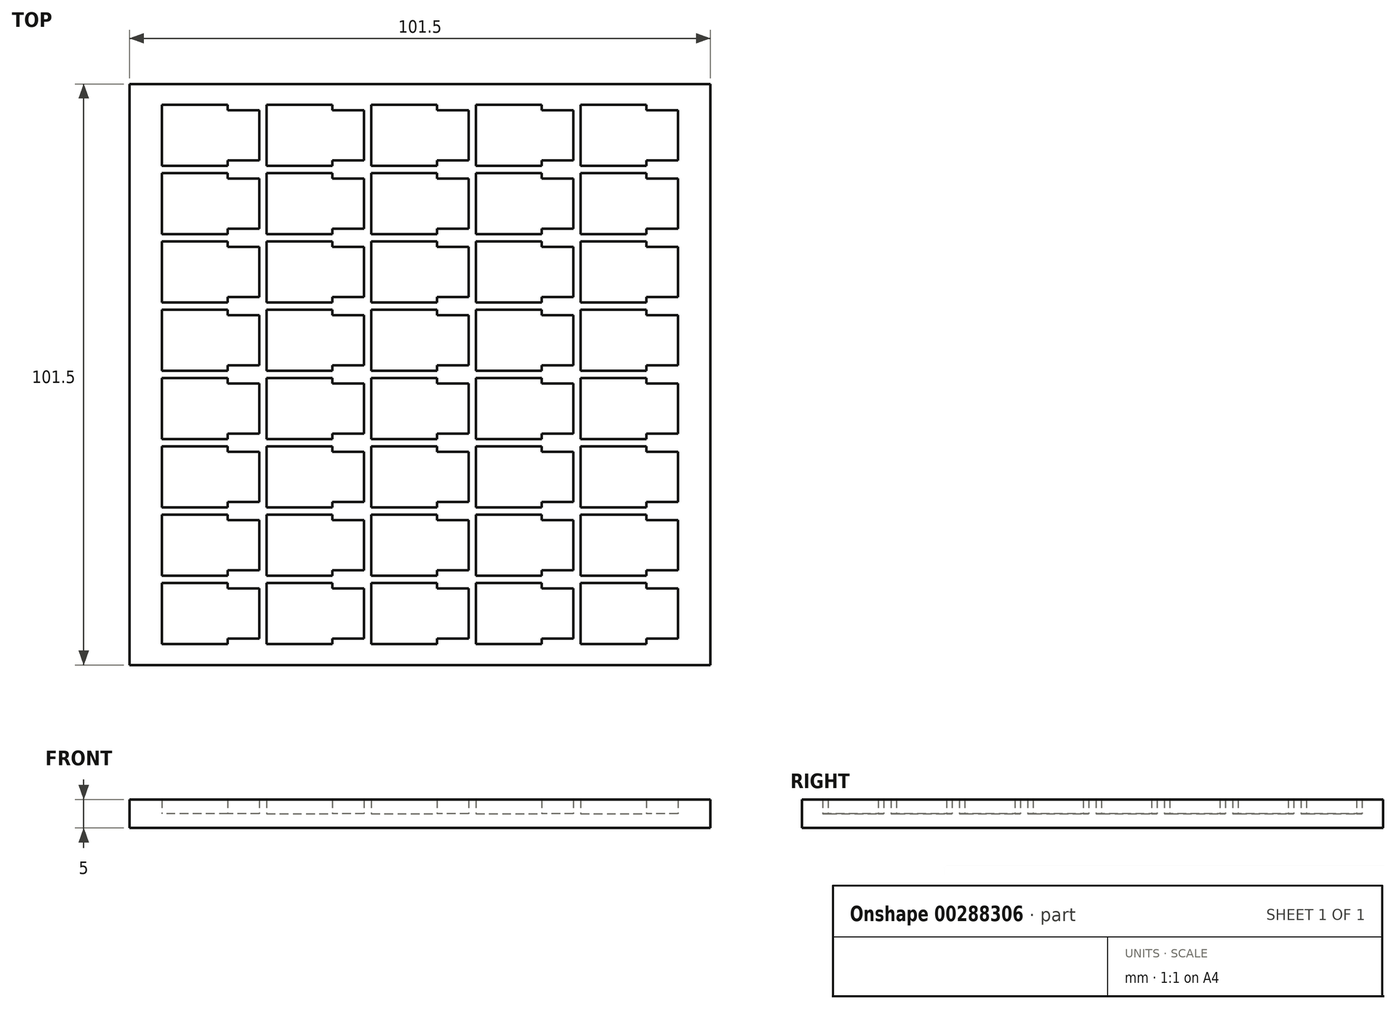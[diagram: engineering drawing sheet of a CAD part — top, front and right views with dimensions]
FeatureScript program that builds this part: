
annotation { "Feature Type Name" : "Feature", "Feature Type Description" : "" }
export const myFeature = defineFeature(function(context is Context, id is Id, definition is map)
    precondition{}
    {
        {
            var Q0;
            Q0=qCreatedBy(makeId("Top.planeOp"),FACE);
            var sketch = newSketch(context, id + "F0", { "sketchPlane" : qUnion([Q0])});
            skLineSegment(sketch, "E0.bottom", {"start": v(50.75, -50.75) * mm, "end": v(-50.75, -50.75) * mm});
            skLineSegment(sketch, "E0.top", {"start": v(50.75, 50.75) * mm, "end": v(-50.75, 50.75) * mm});
            skLineSegment(sketch, "E0.left", {"start": v(50.75, -50.75) * mm, "end": v(50.75, 50.75) * mm});
            skLineSegment(sketch, "E0.right", {"start": v(-50.75, -50.75) * mm, "end": v(-50.75, 50.75) * mm});
            skPoint(sketch, "E0.middle", {"position": v(0, 0) * mm});
            skLineSegment(sketch, "E1", {"start": v(-45.07, 47.12) * mm, "end": v(-45.07, 36.45) * mm});
            skLineSegment(sketch, "E2", {"start": v(-45.07, 36.45) * mm, "end": v(-33.57, 36.45) * mm});
            skLineSegment(sketch, "E3", {"start": v(-33.57, 36.45) * mm, "end": v(-33.57, 37.4) * mm});
            skLineSegment(sketch, "E4", {"start": v(-33.57, 37.4) * mm, "end": v(-28.07, 37.4) * mm});
            skLineSegment(sketch, "E5", {"start": v(-28.07, 37.4) * mm, "end": v(-28.07, 46.16) * mm});
            skLineSegment(sketch, "E6", {"start": v(-28.07, 46.16) * mm, "end": v(-33.57, 46.16) * mm});
            skLineSegment(sketch, "E7", {"start": v(-33.57, 46.16) * mm, "end": v(-33.57, 47.12) * mm});
            skLineSegment(sketch, "E8", {"start": v(-33.57, 47.12) * mm, "end": v(-45.07, 47.12) * mm});
            skLineSegment(sketch, "E9.0.1.0", {"start": v(-33.57, 24.5) * mm, "end": v(-33.57, 25.46) * mm});
            skLineSegment(sketch, "E9.0.1.1", {"start": v(-45.07, 24.5) * mm, "end": v(-33.57, 24.5) * mm});
            skLineSegment(sketch, "E9.0.1.2", {"start": v(-28.07, 25.46) * mm, "end": v(-28.07, 34.23) * mm});
            skLineSegment(sketch, "E9.0.1.3", {"start": v(-33.57, 34.23) * mm, "end": v(-33.57, 35.18) * mm});
            skLineSegment(sketch, "E9.0.1.4", {"start": v(-33.57, 25.46) * mm, "end": v(-28.07, 25.46) * mm});
            skLineSegment(sketch, "E9.0.1.5", {"start": v(-45.07, 35.18) * mm, "end": v(-45.07, 24.5) * mm});
            skLineSegment(sketch, "E9.0.1.6", {"start": v(-33.57, 35.18) * mm, "end": v(-45.07, 35.18) * mm});
            skLineSegment(sketch, "E9.0.1.7", {"start": v(-28.07, 34.23) * mm, "end": v(-33.57, 34.23) * mm});
            skLineSegment(sketch, "E9.0.2.0", {"start": v(-33.57, 12.57) * mm, "end": v(-33.57, 13.53) * mm});
            skLineSegment(sketch, "E9.0.2.1", {"start": v(-45.07, 12.57) * mm, "end": v(-33.57, 12.57) * mm});
            skLineSegment(sketch, "E9.0.2.2", {"start": v(-28.07, 13.53) * mm, "end": v(-28.07, 22.29) * mm});
            skLineSegment(sketch, "E9.0.2.3", {"start": v(-33.57, 22.29) * mm, "end": v(-33.57, 23.24) * mm});
            skLineSegment(sketch, "E9.0.2.4", {"start": v(-33.57, 13.53) * mm, "end": v(-28.07, 13.53) * mm});
            skLineSegment(sketch, "E9.0.2.5", {"start": v(-45.07, 23.24) * mm, "end": v(-45.07, 12.57) * mm});
            skLineSegment(sketch, "E9.0.2.6", {"start": v(-33.57, 23.24) * mm, "end": v(-45.07, 23.24) * mm});
            skLineSegment(sketch, "E9.0.2.7", {"start": v(-28.07, 22.29) * mm, "end": v(-33.57, 22.29) * mm});
            skLineSegment(sketch, "E9.0.3.0", {"start": v(-33.57, 0.63) * mm, "end": v(-33.57, 1.59) * mm});
            skLineSegment(sketch, "E9.0.3.1", {"start": v(-45.07, 0.63) * mm, "end": v(-33.57, 0.63) * mm});
            skLineSegment(sketch, "E9.0.3.2", {"start": v(-28.07, 1.59) * mm, "end": v(-28.07, 10.35) * mm});
            skLineSegment(sketch, "E9.0.3.3", {"start": v(-33.57, 10.35) * mm, "end": v(-33.57, 11.3) * mm});
            skLineSegment(sketch, "E9.0.3.4", {"start": v(-33.57, 1.59) * mm, "end": v(-28.07, 1.59) * mm});
            skLineSegment(sketch, "E9.0.3.5", {"start": v(-45.07, 11.3) * mm, "end": v(-45.07, 0.63) * mm});
            skLineSegment(sketch, "E9.0.3.6", {"start": v(-33.57, 11.3) * mm, "end": v(-45.07, 11.3) * mm});
            skLineSegment(sketch, "E9.0.3.7", {"start": v(-28.07, 10.35) * mm, "end": v(-33.57, 10.35) * mm});
            skLineSegment(sketch, "E9.0.4.0", {"start": v(-33.57, -11.3) * mm, "end": v(-33.57, -10.35) * mm});
            skLineSegment(sketch, "E9.0.4.1", {"start": v(-45.07, -11.3) * mm, "end": v(-33.57, -11.3) * mm});
            skLineSegment(sketch, "E9.0.4.2", {"start": v(-28.07, -10.35) * mm, "end": v(-28.07, -1.59) * mm});
            skLineSegment(sketch, "E9.0.4.3", {"start": v(-33.57, -1.59) * mm, "end": v(-33.57, -0.63) * mm});
            skLineSegment(sketch, "E9.0.4.4", {"start": v(-33.57, -10.35) * mm, "end": v(-28.07, -10.35) * mm});
            skLineSegment(sketch, "E9.0.4.5", {"start": v(-45.07, -0.63) * mm, "end": v(-45.07, -11.3) * mm});
            skLineSegment(sketch, "E9.0.4.6", {"start": v(-33.57, -0.63) * mm, "end": v(-45.07, -0.63) * mm});
            skLineSegment(sketch, "E9.0.4.7", {"start": v(-28.07, -1.59) * mm, "end": v(-33.57, -1.59) * mm});
            skLineSegment(sketch, "E9.0.5.0", {"start": v(-33.57, -23.24) * mm, "end": v(-33.57, -22.29) * mm});
            skLineSegment(sketch, "E9.0.5.1", {"start": v(-45.07, -23.24) * mm, "end": v(-33.57, -23.24) * mm});
            skLineSegment(sketch, "E9.0.5.2", {"start": v(-28.07, -22.29) * mm, "end": v(-28.07, -13.53) * mm});
            skLineSegment(sketch, "E9.0.5.3", {"start": v(-33.57, -13.53) * mm, "end": v(-33.57, -12.57) * mm});
            skLineSegment(sketch, "E9.0.5.4", {"start": v(-33.57, -22.29) * mm, "end": v(-28.07, -22.29) * mm});
            skLineSegment(sketch, "E9.0.5.5", {"start": v(-45.07, -12.57) * mm, "end": v(-45.07, -23.24) * mm});
            skLineSegment(sketch, "E9.0.5.6", {"start": v(-33.57, -12.57) * mm, "end": v(-45.07, -12.57) * mm});
            skLineSegment(sketch, "E9.0.5.7", {"start": v(-28.07, -13.53) * mm, "end": v(-33.57, -13.53) * mm});
            skLineSegment(sketch, "E9.0.6.0", {"start": v(-33.57, -35.18) * mm, "end": v(-33.57, -34.23) * mm});
            skLineSegment(sketch, "E9.0.6.1", {"start": v(-45.07, -35.18) * mm, "end": v(-33.57, -35.18) * mm});
            skLineSegment(sketch, "E9.0.6.2", {"start": v(-28.07, -34.23) * mm, "end": v(-28.07, -25.46) * mm});
            skLineSegment(sketch, "E9.0.6.3", {"start": v(-33.57, -25.46) * mm, "end": v(-33.57, -24.51) * mm});
            skLineSegment(sketch, "E9.0.6.4", {"start": v(-33.57, -34.23) * mm, "end": v(-28.07, -34.23) * mm});
            skLineSegment(sketch, "E9.0.6.5", {"start": v(-45.07, -24.51) * mm, "end": v(-45.07, -35.18) * mm});
            skLineSegment(sketch, "E9.0.6.6", {"start": v(-33.57, -24.51) * mm, "end": v(-45.07, -24.51) * mm});
            skLineSegment(sketch, "E9.0.6.7", {"start": v(-28.07, -25.46) * mm, "end": v(-33.57, -25.46) * mm});
            skLineSegment(sketch, "E9.0.7.0", {"start": v(-33.57, -47.12) * mm, "end": v(-33.57, -46.16) * mm});
            skLineSegment(sketch, "E9.0.7.1", {"start": v(-45.07, -47.12) * mm, "end": v(-33.57, -47.12) * mm});
            skLineSegment(sketch, "E9.0.7.2", {"start": v(-28.07, -46.16) * mm, "end": v(-28.07, -37.4) * mm});
            skLineSegment(sketch, "E9.0.7.3", {"start": v(-33.57, -37.4) * mm, "end": v(-33.57, -36.45) * mm});
            skLineSegment(sketch, "E9.0.7.4", {"start": v(-33.57, -46.16) * mm, "end": v(-28.07, -46.16) * mm});
            skLineSegment(sketch, "E9.0.7.5", {"start": v(-45.07, -36.45) * mm, "end": v(-45.07, -47.12) * mm});
            skLineSegment(sketch, "E9.0.7.6", {"start": v(-33.57, -36.45) * mm, "end": v(-45.07, -36.45) * mm});
            skLineSegment(sketch, "E9.0.7.7", {"start": v(-28.07, -37.4) * mm, "end": v(-33.57, -37.4) * mm});
            skLineSegment(sketch, "E9.1.0.0", {"start": v(-15.29, 36.45) * mm, "end": v(-15.29, 37.4) * mm});
            skLineSegment(sketch, "E9.1.0.1", {"start": v(-26.79, 36.45) * mm, "end": v(-15.29, 36.45) * mm});
            skLineSegment(sketch, "E9.1.0.2", {"start": v(-9.79, 37.4) * mm, "end": v(-9.79, 46.16) * mm});
            skLineSegment(sketch, "E9.1.0.3", {"start": v(-15.29, 46.16) * mm, "end": v(-15.29, 47.12) * mm});
            skLineSegment(sketch, "E9.1.0.4", {"start": v(-15.29, 37.4) * mm, "end": v(-9.79, 37.4) * mm});
            skLineSegment(sketch, "E9.1.0.5", {"start": v(-26.79, 47.12) * mm, "end": v(-26.79, 36.45) * mm});
            skLineSegment(sketch, "E9.1.0.6", {"start": v(-15.29, 47.12) * mm, "end": v(-26.79, 47.12) * mm});
            skLineSegment(sketch, "E9.1.0.7", {"start": v(-9.79, 46.16) * mm, "end": v(-15.29, 46.16) * mm});
            skLineSegment(sketch, "E9.1.1.0", {"start": v(-15.29, 24.5) * mm, "end": v(-15.29, 25.46) * mm});
            skLineSegment(sketch, "E9.1.1.1", {"start": v(-26.79, 24.5) * mm, "end": v(-15.29, 24.5) * mm});
            skLineSegment(sketch, "E9.1.1.2", {"start": v(-9.79, 25.46) * mm, "end": v(-9.79, 34.23) * mm});
            skLineSegment(sketch, "E9.1.1.3", {"start": v(-15.29, 34.23) * mm, "end": v(-15.29, 35.18) * mm});
            skLineSegment(sketch, "E9.1.1.4", {"start": v(-15.29, 25.46) * mm, "end": v(-9.79, 25.46) * mm});
            skLineSegment(sketch, "E9.1.1.5", {"start": v(-26.79, 35.18) * mm, "end": v(-26.79, 24.5) * mm});
            skLineSegment(sketch, "E9.1.1.6", {"start": v(-15.29, 35.18) * mm, "end": v(-26.79, 35.18) * mm});
            skLineSegment(sketch, "E9.1.1.7", {"start": v(-9.79, 34.23) * mm, "end": v(-15.29, 34.23) * mm});
            skLineSegment(sketch, "E9.1.2.0", {"start": v(-15.29, 12.57) * mm, "end": v(-15.29, 13.53) * mm});
            skLineSegment(sketch, "E9.1.2.1", {"start": v(-26.79, 12.57) * mm, "end": v(-15.29, 12.57) * mm});
            skLineSegment(sketch, "E9.1.2.2", {"start": v(-9.79, 13.53) * mm, "end": v(-9.79, 22.29) * mm});
            skLineSegment(sketch, "E9.1.2.3", {"start": v(-15.29, 22.29) * mm, "end": v(-15.29, 23.24) * mm});
            skLineSegment(sketch, "E9.1.2.4", {"start": v(-15.29, 13.53) * mm, "end": v(-9.79, 13.53) * mm});
            skLineSegment(sketch, "E9.1.2.5", {"start": v(-26.79, 23.24) * mm, "end": v(-26.79, 12.57) * mm});
            skLineSegment(sketch, "E9.1.2.6", {"start": v(-15.29, 23.24) * mm, "end": v(-26.79, 23.24) * mm});
            skLineSegment(sketch, "E9.1.2.7", {"start": v(-9.79, 22.29) * mm, "end": v(-15.29, 22.29) * mm});
            skLineSegment(sketch, "E9.1.3.0", {"start": v(-15.29, 0.63) * mm, "end": v(-15.29, 1.59) * mm});
            skLineSegment(sketch, "E9.1.3.1", {"start": v(-26.79, 0.63) * mm, "end": v(-15.29, 0.63) * mm});
            skLineSegment(sketch, "E9.1.3.2", {"start": v(-9.79, 1.59) * mm, "end": v(-9.79, 10.35) * mm});
            skLineSegment(sketch, "E9.1.3.3", {"start": v(-15.29, 10.35) * mm, "end": v(-15.29, 11.3) * mm});
            skLineSegment(sketch, "E9.1.3.4", {"start": v(-15.29, 1.59) * mm, "end": v(-9.79, 1.59) * mm});
            skLineSegment(sketch, "E9.1.3.5", {"start": v(-26.79, 11.3) * mm, "end": v(-26.79, 0.63) * mm});
            skLineSegment(sketch, "E9.1.3.6", {"start": v(-15.29, 11.3) * mm, "end": v(-26.79, 11.3) * mm});
            skLineSegment(sketch, "E9.1.3.7", {"start": v(-9.79, 10.35) * mm, "end": v(-15.29, 10.35) * mm});
            skLineSegment(sketch, "E9.1.4.0", {"start": v(-15.29, -11.3) * mm, "end": v(-15.29, -10.35) * mm});
            skLineSegment(sketch, "E9.1.4.1", {"start": v(-26.79, -11.3) * mm, "end": v(-15.29, -11.3) * mm});
            skLineSegment(sketch, "E9.1.4.2", {"start": v(-9.79, -10.35) * mm, "end": v(-9.79, -1.59) * mm});
            skLineSegment(sketch, "E9.1.4.3", {"start": v(-15.29, -1.59) * mm, "end": v(-15.29, -0.63) * mm});
            skLineSegment(sketch, "E9.1.4.4", {"start": v(-15.29, -10.35) * mm, "end": v(-9.79, -10.35) * mm});
            skLineSegment(sketch, "E9.1.4.5", {"start": v(-26.79, -0.63) * mm, "end": v(-26.79, -11.3) * mm});
            skLineSegment(sketch, "E9.1.4.6", {"start": v(-15.29, -0.63) * mm, "end": v(-26.79, -0.63) * mm});
            skLineSegment(sketch, "E9.1.4.7", {"start": v(-9.79, -1.59) * mm, "end": v(-15.29, -1.59) * mm});
            skLineSegment(sketch, "E9.1.5.0", {"start": v(-15.29, -23.24) * mm, "end": v(-15.29, -22.29) * mm});
            skLineSegment(sketch, "E9.1.5.1", {"start": v(-26.79, -23.24) * mm, "end": v(-15.29, -23.24) * mm});
            skLineSegment(sketch, "E9.1.5.2", {"start": v(-9.79, -22.29) * mm, "end": v(-9.79, -13.53) * mm});
            skLineSegment(sketch, "E9.1.5.3", {"start": v(-15.29, -13.53) * mm, "end": v(-15.29, -12.57) * mm});
            skLineSegment(sketch, "E9.1.5.4", {"start": v(-15.29, -22.29) * mm, "end": v(-9.79, -22.29) * mm});
            skLineSegment(sketch, "E9.1.5.5", {"start": v(-26.79, -12.57) * mm, "end": v(-26.79, -23.24) * mm});
            skLineSegment(sketch, "E9.1.5.6", {"start": v(-15.29, -12.57) * mm, "end": v(-26.79, -12.57) * mm});
            skLineSegment(sketch, "E9.1.5.7", {"start": v(-9.79, -13.53) * mm, "end": v(-15.29, -13.53) * mm});
            skLineSegment(sketch, "E9.1.6.0", {"start": v(-15.29, -35.18) * mm, "end": v(-15.29, -34.23) * mm});
            skLineSegment(sketch, "E9.1.6.1", {"start": v(-26.79, -35.18) * mm, "end": v(-15.29, -35.18) * mm});
            skLineSegment(sketch, "E9.1.6.2", {"start": v(-9.79, -34.23) * mm, "end": v(-9.79, -25.46) * mm});
            skLineSegment(sketch, "E9.1.6.3", {"start": v(-15.29, -25.46) * mm, "end": v(-15.29, -24.51) * mm});
            skLineSegment(sketch, "E9.1.6.4", {"start": v(-15.29, -34.23) * mm, "end": v(-9.79, -34.23) * mm});
            skLineSegment(sketch, "E9.1.6.5", {"start": v(-26.79, -24.51) * mm, "end": v(-26.79, -35.18) * mm});
            skLineSegment(sketch, "E9.1.6.6", {"start": v(-15.29, -24.51) * mm, "end": v(-26.79, -24.51) * mm});
            skLineSegment(sketch, "E9.1.6.7", {"start": v(-9.79, -25.46) * mm, "end": v(-15.29, -25.46) * mm});
            skLineSegment(sketch, "E9.1.7.0", {"start": v(-15.29, -47.12) * mm, "end": v(-15.29, -46.16) * mm});
            skLineSegment(sketch, "E9.1.7.1", {"start": v(-26.79, -47.12) * mm, "end": v(-15.29, -47.12) * mm});
            skLineSegment(sketch, "E9.1.7.2", {"start": v(-9.79, -46.16) * mm, "end": v(-9.79, -37.4) * mm});
            skLineSegment(sketch, "E9.1.7.3", {"start": v(-15.29, -37.4) * mm, "end": v(-15.29, -36.45) * mm});
            skLineSegment(sketch, "E9.1.7.4", {"start": v(-15.29, -46.16) * mm, "end": v(-9.79, -46.16) * mm});
            skLineSegment(sketch, "E9.1.7.5", {"start": v(-26.79, -36.45) * mm, "end": v(-26.79, -47.12) * mm});
            skLineSegment(sketch, "E9.1.7.6", {"start": v(-15.29, -36.45) * mm, "end": v(-26.79, -36.45) * mm});
            skLineSegment(sketch, "E9.1.7.7", {"start": v(-9.79, -37.4) * mm, "end": v(-15.29, -37.4) * mm});
            skLineSegment(sketch, "E9.2.0.0", {"start": v(3, 36.45) * mm, "end": v(3, 37.4) * mm});
            skLineSegment(sketch, "E9.2.0.1", {"start": v(-8.5, 36.45) * mm, "end": v(3, 36.45) * mm});
            skLineSegment(sketch, "E9.2.0.2", {"start": v(8.5, 37.4) * mm, "end": v(8.5, 46.16) * mm});
            skLineSegment(sketch, "E9.2.0.3", {"start": v(3, 46.16) * mm, "end": v(3, 47.12) * mm});
            skLineSegment(sketch, "E9.2.0.4", {"start": v(3, 37.4) * mm, "end": v(8.5, 37.4) * mm});
            skLineSegment(sketch, "E9.2.0.5", {"start": v(-8.5, 47.12) * mm, "end": v(-8.5, 36.45) * mm});
            skLineSegment(sketch, "E9.2.0.6", {"start": v(3, 47.12) * mm, "end": v(-8.5, 47.12) * mm});
            skLineSegment(sketch, "E9.2.0.7", {"start": v(8.5, 46.16) * mm, "end": v(3, 46.16) * mm});
            skLineSegment(sketch, "E9.2.1.0", {"start": v(3, 24.5) * mm, "end": v(3, 25.46) * mm});
            skLineSegment(sketch, "E9.2.1.1", {"start": v(-8.5, 24.5) * mm, "end": v(3, 24.5) * mm});
            skLineSegment(sketch, "E9.2.1.2", {"start": v(8.5, 25.46) * mm, "end": v(8.5, 34.23) * mm});
            skLineSegment(sketch, "E9.2.1.3", {"start": v(3, 34.23) * mm, "end": v(3, 35.18) * mm});
            skLineSegment(sketch, "E9.2.1.4", {"start": v(3, 25.46) * mm, "end": v(8.5, 25.46) * mm});
            skLineSegment(sketch, "E9.2.1.5", {"start": v(-8.5, 35.18) * mm, "end": v(-8.5, 24.5) * mm});
            skLineSegment(sketch, "E9.2.1.6", {"start": v(3, 35.18) * mm, "end": v(-8.5, 35.18) * mm});
            skLineSegment(sketch, "E9.2.1.7", {"start": v(8.5, 34.23) * mm, "end": v(3, 34.23) * mm});
            skLineSegment(sketch, "E9.2.2.0", {"start": v(3, 12.57) * mm, "end": v(3, 13.53) * mm});
            skLineSegment(sketch, "E9.2.2.1", {"start": v(-8.5, 12.57) * mm, "end": v(3, 12.57) * mm});
            skLineSegment(sketch, "E9.2.2.2", {"start": v(8.5, 13.53) * mm, "end": v(8.5, 22.29) * mm});
            skLineSegment(sketch, "E9.2.2.3", {"start": v(3, 22.29) * mm, "end": v(3, 23.24) * mm});
            skLineSegment(sketch, "E9.2.2.4", {"start": v(3, 13.53) * mm, "end": v(8.5, 13.53) * mm});
            skLineSegment(sketch, "E9.2.2.5", {"start": v(-8.5, 23.24) * mm, "end": v(-8.5, 12.57) * mm});
            skLineSegment(sketch, "E9.2.2.6", {"start": v(3, 23.24) * mm, "end": v(-8.5, 23.24) * mm});
            skLineSegment(sketch, "E9.2.2.7", {"start": v(8.5, 22.29) * mm, "end": v(3, 22.29) * mm});
            skLineSegment(sketch, "E9.2.3.0", {"start": v(3, 0.63) * mm, "end": v(3, 1.59) * mm});
            skLineSegment(sketch, "E9.2.3.1", {"start": v(-8.5, 0.63) * mm, "end": v(3, 0.63) * mm});
            skLineSegment(sketch, "E9.2.3.2", {"start": v(8.5, 1.59) * mm, "end": v(8.5, 10.35) * mm});
            skLineSegment(sketch, "E9.2.3.3", {"start": v(3, 10.35) * mm, "end": v(3, 11.3) * mm});
            skLineSegment(sketch, "E9.2.3.4", {"start": v(3, 1.59) * mm, "end": v(8.5, 1.59) * mm});
            skLineSegment(sketch, "E9.2.3.5", {"start": v(-8.5, 11.3) * mm, "end": v(-8.5, 0.63) * mm});
            skLineSegment(sketch, "E9.2.3.6", {"start": v(3, 11.3) * mm, "end": v(-8.5, 11.3) * mm});
            skLineSegment(sketch, "E9.2.3.7", {"start": v(8.5, 10.35) * mm, "end": v(3, 10.35) * mm});
            skLineSegment(sketch, "E9.2.4.0", {"start": v(3, -11.3) * mm, "end": v(3, -10.35) * mm});
            skLineSegment(sketch, "E9.2.4.1", {"start": v(-8.5, -11.3) * mm, "end": v(3, -11.3) * mm});
            skLineSegment(sketch, "E9.2.4.2", {"start": v(8.5, -10.35) * mm, "end": v(8.5, -1.59) * mm});
            skLineSegment(sketch, "E9.2.4.3", {"start": v(3, -1.59) * mm, "end": v(3, -0.63) * mm});
            skLineSegment(sketch, "E9.2.4.4", {"start": v(3, -10.35) * mm, "end": v(8.5, -10.35) * mm});
            skLineSegment(sketch, "E9.2.4.5", {"start": v(-8.5, -0.63) * mm, "end": v(-8.5, -11.3) * mm});
            skLineSegment(sketch, "E9.2.4.6", {"start": v(3, -0.63) * mm, "end": v(-8.5, -0.63) * mm});
            skLineSegment(sketch, "E9.2.4.7", {"start": v(8.5, -1.59) * mm, "end": v(3, -1.59) * mm});
            skLineSegment(sketch, "E9.2.5.0", {"start": v(3, -23.24) * mm, "end": v(3, -22.29) * mm});
            skLineSegment(sketch, "E9.2.5.1", {"start": v(-8.5, -23.24) * mm, "end": v(3, -23.24) * mm});
            skLineSegment(sketch, "E9.2.5.2", {"start": v(8.5, -22.29) * mm, "end": v(8.5, -13.53) * mm});
            skLineSegment(sketch, "E9.2.5.3", {"start": v(3, -13.53) * mm, "end": v(3, -12.57) * mm});
            skLineSegment(sketch, "E9.2.5.4", {"start": v(3, -22.29) * mm, "end": v(8.5, -22.29) * mm});
            skLineSegment(sketch, "E9.2.5.5", {"start": v(-8.5, -12.57) * mm, "end": v(-8.5, -23.24) * mm});
            skLineSegment(sketch, "E9.2.5.6", {"start": v(3, -12.57) * mm, "end": v(-8.5, -12.57) * mm});
            skLineSegment(sketch, "E9.2.5.7", {"start": v(8.5, -13.53) * mm, "end": v(3, -13.53) * mm});
            skLineSegment(sketch, "E9.2.6.0", {"start": v(3, -35.18) * mm, "end": v(3, -34.23) * mm});
            skLineSegment(sketch, "E9.2.6.1", {"start": v(-8.5, -35.18) * mm, "end": v(3, -35.18) * mm});
            skLineSegment(sketch, "E9.2.6.2", {"start": v(8.5, -34.23) * mm, "end": v(8.5, -25.46) * mm});
            skLineSegment(sketch, "E9.2.6.3", {"start": v(3, -25.46) * mm, "end": v(3, -24.51) * mm});
            skLineSegment(sketch, "E9.2.6.4", {"start": v(3, -34.23) * mm, "end": v(8.5, -34.23) * mm});
            skLineSegment(sketch, "E9.2.6.5", {"start": v(-8.5, -24.51) * mm, "end": v(-8.5, -35.18) * mm});
            skLineSegment(sketch, "E9.2.6.6", {"start": v(3, -24.51) * mm, "end": v(-8.5, -24.51) * mm});
            skLineSegment(sketch, "E9.2.6.7", {"start": v(8.5, -25.46) * mm, "end": v(3, -25.46) * mm});
            skLineSegment(sketch, "E9.2.7.0", {"start": v(3, -47.12) * mm, "end": v(3, -46.16) * mm});
            skLineSegment(sketch, "E9.2.7.1", {"start": v(-8.5, -47.12) * mm, "end": v(3, -47.12) * mm});
            skLineSegment(sketch, "E9.2.7.2", {"start": v(8.5, -46.16) * mm, "end": v(8.5, -37.4) * mm});
            skLineSegment(sketch, "E9.2.7.3", {"start": v(3, -37.4) * mm, "end": v(3, -36.45) * mm});
            skLineSegment(sketch, "E9.2.7.4", {"start": v(3, -46.16) * mm, "end": v(8.5, -46.16) * mm});
            skLineSegment(sketch, "E9.2.7.5", {"start": v(-8.5, -36.45) * mm, "end": v(-8.5, -47.12) * mm});
            skLineSegment(sketch, "E9.2.7.6", {"start": v(3, -36.45) * mm, "end": v(-8.5, -36.45) * mm});
            skLineSegment(sketch, "E9.2.7.7", {"start": v(8.5, -37.4) * mm, "end": v(3, -37.4) * mm});
            skLineSegment(sketch, "E9.3.0.0", {"start": v(21.3, 36.45) * mm, "end": v(21.3, 37.4) * mm});
            skLineSegment(sketch, "E9.3.0.1", {"start": v(9.8, 36.45) * mm, "end": v(21.3, 36.45) * mm});
            skLineSegment(sketch, "E9.3.0.2", {"start": v(26.8, 37.4) * mm, "end": v(26.8, 46.16) * mm});
            skLineSegment(sketch, "E9.3.0.3", {"start": v(21.3, 46.16) * mm, "end": v(21.3, 47.12) * mm});
            skLineSegment(sketch, "E9.3.0.4", {"start": v(21.3, 37.4) * mm, "end": v(26.8, 37.4) * mm});
            skLineSegment(sketch, "E9.3.0.5", {"start": v(9.8, 47.12) * mm, "end": v(9.8, 36.45) * mm});
            skLineSegment(sketch, "E9.3.0.6", {"start": v(21.3, 47.12) * mm, "end": v(9.8, 47.12) * mm});
            skLineSegment(sketch, "E9.3.0.7", {"start": v(26.8, 46.16) * mm, "end": v(21.3, 46.16) * mm});
            skLineSegment(sketch, "E9.3.1.0", {"start": v(21.3, 24.5) * mm, "end": v(21.3, 25.46) * mm});
            skLineSegment(sketch, "E9.3.1.1", {"start": v(9.8, 24.5) * mm, "end": v(21.3, 24.5) * mm});
            skLineSegment(sketch, "E9.3.1.2", {"start": v(26.8, 25.46) * mm, "end": v(26.8, 34.23) * mm});
            skLineSegment(sketch, "E9.3.1.3", {"start": v(21.3, 34.23) * mm, "end": v(21.3, 35.18) * mm});
            skLineSegment(sketch, "E9.3.1.4", {"start": v(21.3, 25.46) * mm, "end": v(26.8, 25.46) * mm});
            skLineSegment(sketch, "E9.3.1.5", {"start": v(9.8, 35.18) * mm, "end": v(9.8, 24.5) * mm});
            skLineSegment(sketch, "E9.3.1.6", {"start": v(21.3, 35.18) * mm, "end": v(9.8, 35.18) * mm});
            skLineSegment(sketch, "E9.3.1.7", {"start": v(26.8, 34.23) * mm, "end": v(21.3, 34.23) * mm});
            skLineSegment(sketch, "E9.3.2.0", {"start": v(21.3, 12.57) * mm, "end": v(21.3, 13.53) * mm});
            skLineSegment(sketch, "E9.3.2.1", {"start": v(9.8, 12.57) * mm, "end": v(21.3, 12.57) * mm});
            skLineSegment(sketch, "E9.3.2.2", {"start": v(26.8, 13.53) * mm, "end": v(26.8, 22.29) * mm});
            skLineSegment(sketch, "E9.3.2.3", {"start": v(21.3, 22.29) * mm, "end": v(21.3, 23.24) * mm});
            skLineSegment(sketch, "E9.3.2.4", {"start": v(21.3, 13.53) * mm, "end": v(26.8, 13.53) * mm});
            skLineSegment(sketch, "E9.3.2.5", {"start": v(9.8, 23.24) * mm, "end": v(9.8, 12.57) * mm});
            skLineSegment(sketch, "E9.3.2.6", {"start": v(21.3, 23.24) * mm, "end": v(9.8, 23.24) * mm});
            skLineSegment(sketch, "E9.3.2.7", {"start": v(26.8, 22.29) * mm, "end": v(21.3, 22.29) * mm});
            skLineSegment(sketch, "E9.3.3.0", {"start": v(21.3, 0.63) * mm, "end": v(21.3, 1.59) * mm});
            skLineSegment(sketch, "E9.3.3.1", {"start": v(9.8, 0.63) * mm, "end": v(21.3, 0.63) * mm});
            skLineSegment(sketch, "E9.3.3.2", {"start": v(26.8, 1.59) * mm, "end": v(26.8, 10.35) * mm});
            skLineSegment(sketch, "E9.3.3.3", {"start": v(21.3, 10.35) * mm, "end": v(21.3, 11.3) * mm});
            skLineSegment(sketch, "E9.3.3.4", {"start": v(21.3, 1.59) * mm, "end": v(26.8, 1.59) * mm});
            skLineSegment(sketch, "E9.3.3.5", {"start": v(9.8, 11.3) * mm, "end": v(9.8, 0.63) * mm});
            skLineSegment(sketch, "E9.3.3.6", {"start": v(21.3, 11.3) * mm, "end": v(9.8, 11.3) * mm});
            skLineSegment(sketch, "E9.3.3.7", {"start": v(26.8, 10.35) * mm, "end": v(21.3, 10.35) * mm});
            skLineSegment(sketch, "E9.3.4.0", {"start": v(21.3, -11.3) * mm, "end": v(21.3, -10.35) * mm});
            skLineSegment(sketch, "E9.3.4.1", {"start": v(9.8, -11.3) * mm, "end": v(21.3, -11.3) * mm});
            skLineSegment(sketch, "E9.3.4.2", {"start": v(26.8, -10.35) * mm, "end": v(26.8, -1.59) * mm});
            skLineSegment(sketch, "E9.3.4.3", {"start": v(21.3, -1.59) * mm, "end": v(21.3, -0.63) * mm});
            skLineSegment(sketch, "E9.3.4.4", {"start": v(21.3, -10.35) * mm, "end": v(26.8, -10.35) * mm});
            skLineSegment(sketch, "E9.3.4.5", {"start": v(9.8, -0.63) * mm, "end": v(9.8, -11.3) * mm});
            skLineSegment(sketch, "E9.3.4.6", {"start": v(21.3, -0.63) * mm, "end": v(9.8, -0.63) * mm});
            skLineSegment(sketch, "E9.3.4.7", {"start": v(26.8, -1.59) * mm, "end": v(21.3, -1.59) * mm});
            skLineSegment(sketch, "E9.3.5.0", {"start": v(21.3, -23.24) * mm, "end": v(21.3, -22.29) * mm});
            skLineSegment(sketch, "E9.3.5.1", {"start": v(9.8, -23.24) * mm, "end": v(21.3, -23.24) * mm});
            skLineSegment(sketch, "E9.3.5.2", {"start": v(26.8, -22.29) * mm, "end": v(26.8, -13.53) * mm});
            skLineSegment(sketch, "E9.3.5.3", {"start": v(21.3, -13.53) * mm, "end": v(21.3, -12.57) * mm});
            skLineSegment(sketch, "E9.3.5.4", {"start": v(21.3, -22.29) * mm, "end": v(26.8, -22.29) * mm});
            skLineSegment(sketch, "E9.3.5.5", {"start": v(9.8, -12.57) * mm, "end": v(9.8, -23.24) * mm});
            skLineSegment(sketch, "E9.3.5.6", {"start": v(21.3, -12.57) * mm, "end": v(9.8, -12.57) * mm});
            skLineSegment(sketch, "E9.3.5.7", {"start": v(26.8, -13.53) * mm, "end": v(21.3, -13.53) * mm});
            skLineSegment(sketch, "E9.3.6.0", {"start": v(21.3, -35.18) * mm, "end": v(21.3, -34.23) * mm});
            skLineSegment(sketch, "E9.3.6.1", {"start": v(9.8, -35.18) * mm, "end": v(21.3, -35.18) * mm});
            skLineSegment(sketch, "E9.3.6.2", {"start": v(26.8, -34.23) * mm, "end": v(26.8, -25.46) * mm});
            skLineSegment(sketch, "E9.3.6.3", {"start": v(21.3, -25.46) * mm, "end": v(21.3, -24.51) * mm});
            skLineSegment(sketch, "E9.3.6.4", {"start": v(21.3, -34.23) * mm, "end": v(26.8, -34.23) * mm});
            skLineSegment(sketch, "E9.3.6.5", {"start": v(9.8, -24.51) * mm, "end": v(9.8, -35.18) * mm});
            skLineSegment(sketch, "E9.3.6.6", {"start": v(21.3, -24.51) * mm, "end": v(9.8, -24.51) * mm});
            skLineSegment(sketch, "E9.3.6.7", {"start": v(26.8, -25.46) * mm, "end": v(21.3, -25.46) * mm});
            skLineSegment(sketch, "E9.3.7.0", {"start": v(21.3, -47.12) * mm, "end": v(21.3, -46.16) * mm});
            skLineSegment(sketch, "E9.3.7.1", {"start": v(9.8, -47.12) * mm, "end": v(21.3, -47.12) * mm});
            skLineSegment(sketch, "E9.3.7.2", {"start": v(26.8, -46.16) * mm, "end": v(26.8, -37.4) * mm});
            skLineSegment(sketch, "E9.3.7.3", {"start": v(21.3, -37.4) * mm, "end": v(21.3, -36.45) * mm});
            skLineSegment(sketch, "E9.3.7.4", {"start": v(21.3, -46.16) * mm, "end": v(26.8, -46.16) * mm});
            skLineSegment(sketch, "E9.3.7.5", {"start": v(9.8, -36.45) * mm, "end": v(9.8, -47.12) * mm});
            skLineSegment(sketch, "E9.3.7.6", {"start": v(21.3, -36.45) * mm, "end": v(9.8, -36.45) * mm});
            skLineSegment(sketch, "E9.3.7.7", {"start": v(26.8, -37.4) * mm, "end": v(21.3, -37.4) * mm});
            skLineSegment(sketch, "E9.4.0.0", {"start": v(39.58, 36.45) * mm, "end": v(39.58, 37.4) * mm});
            skLineSegment(sketch, "E9.4.0.1", {"start": v(28.08, 36.45) * mm, "end": v(39.58, 36.45) * mm});
            skLineSegment(sketch, "E9.4.0.2", {"start": v(45.08, 37.4) * mm, "end": v(45.08, 46.16) * mm});
            skLineSegment(sketch, "E9.4.0.3", {"start": v(39.58, 46.16) * mm, "end": v(39.58, 47.12) * mm});
            skLineSegment(sketch, "E9.4.0.4", {"start": v(39.58, 37.4) * mm, "end": v(45.08, 37.4) * mm});
            skLineSegment(sketch, "E9.4.0.5", {"start": v(28.08, 47.12) * mm, "end": v(28.08, 36.45) * mm});
            skLineSegment(sketch, "E9.4.0.6", {"start": v(39.58, 47.12) * mm, "end": v(28.08, 47.12) * mm});
            skLineSegment(sketch, "E9.4.0.7", {"start": v(45.08, 46.16) * mm, "end": v(39.58, 46.16) * mm});
            skLineSegment(sketch, "E9.4.1.0", {"start": v(39.58, 24.5) * mm, "end": v(39.58, 25.46) * mm});
            skLineSegment(sketch, "E9.4.1.1", {"start": v(28.08, 24.5) * mm, "end": v(39.58, 24.5) * mm});
            skLineSegment(sketch, "E9.4.1.2", {"start": v(45.08, 25.46) * mm, "end": v(45.08, 34.23) * mm});
            skLineSegment(sketch, "E9.4.1.3", {"start": v(39.58, 34.23) * mm, "end": v(39.58, 35.18) * mm});
            skLineSegment(sketch, "E9.4.1.4", {"start": v(39.58, 25.46) * mm, "end": v(45.08, 25.46) * mm});
            skLineSegment(sketch, "E9.4.1.5", {"start": v(28.08, 35.18) * mm, "end": v(28.08, 24.5) * mm});
            skLineSegment(sketch, "E9.4.1.6", {"start": v(39.58, 35.18) * mm, "end": v(28.08, 35.18) * mm});
            skLineSegment(sketch, "E9.4.1.7", {"start": v(45.08, 34.23) * mm, "end": v(39.58, 34.23) * mm});
            skLineSegment(sketch, "E9.4.2.0", {"start": v(39.58, 12.57) * mm, "end": v(39.58, 13.53) * mm});
            skLineSegment(sketch, "E9.4.2.1", {"start": v(28.08, 12.57) * mm, "end": v(39.58, 12.57) * mm});
            skLineSegment(sketch, "E9.4.2.2", {"start": v(45.08, 13.53) * mm, "end": v(45.08, 22.29) * mm});
            skLineSegment(sketch, "E9.4.2.3", {"start": v(39.58, 22.29) * mm, "end": v(39.58, 23.24) * mm});
            skLineSegment(sketch, "E9.4.2.4", {"start": v(39.58, 13.53) * mm, "end": v(45.08, 13.53) * mm});
            skLineSegment(sketch, "E9.4.2.5", {"start": v(28.08, 23.24) * mm, "end": v(28.08, 12.57) * mm});
            skLineSegment(sketch, "E9.4.2.6", {"start": v(39.58, 23.24) * mm, "end": v(28.08, 23.24) * mm});
            skLineSegment(sketch, "E9.4.2.7", {"start": v(45.08, 22.29) * mm, "end": v(39.58, 22.29) * mm});
            skLineSegment(sketch, "E9.4.3.0", {"start": v(39.58, 0.63) * mm, "end": v(39.58, 1.59) * mm});
            skLineSegment(sketch, "E9.4.3.1", {"start": v(28.08, 0.63) * mm, "end": v(39.58, 0.63) * mm});
            skLineSegment(sketch, "E9.4.3.2", {"start": v(45.08, 1.59) * mm, "end": v(45.08, 10.35) * mm});
            skLineSegment(sketch, "E9.4.3.3", {"start": v(39.58, 10.35) * mm, "end": v(39.58, 11.3) * mm});
            skLineSegment(sketch, "E9.4.3.4", {"start": v(39.58, 1.59) * mm, "end": v(45.08, 1.59) * mm});
            skLineSegment(sketch, "E9.4.3.5", {"start": v(28.08, 11.3) * mm, "end": v(28.08, 0.63) * mm});
            skLineSegment(sketch, "E9.4.3.6", {"start": v(39.58, 11.3) * mm, "end": v(28.08, 11.3) * mm});
            skLineSegment(sketch, "E9.4.3.7", {"start": v(45.08, 10.35) * mm, "end": v(39.58, 10.35) * mm});
            skLineSegment(sketch, "E9.4.4.0", {"start": v(39.58, -11.3) * mm, "end": v(39.58, -10.35) * mm});
            skLineSegment(sketch, "E9.4.4.1", {"start": v(28.08, -11.3) * mm, "end": v(39.58, -11.3) * mm});
            skLineSegment(sketch, "E9.4.4.2", {"start": v(45.08, -10.35) * mm, "end": v(45.08, -1.59) * mm});
            skLineSegment(sketch, "E9.4.4.3", {"start": v(39.58, -1.59) * mm, "end": v(39.58, -0.63) * mm});
            skLineSegment(sketch, "E9.4.4.4", {"start": v(39.58, -10.35) * mm, "end": v(45.08, -10.35) * mm});
            skLineSegment(sketch, "E9.4.4.5", {"start": v(28.08, -0.63) * mm, "end": v(28.08, -11.3) * mm});
            skLineSegment(sketch, "E9.4.4.6", {"start": v(39.58, -0.63) * mm, "end": v(28.08, -0.63) * mm});
            skLineSegment(sketch, "E9.4.4.7", {"start": v(45.08, -1.59) * mm, "end": v(39.58, -1.59) * mm});
            skLineSegment(sketch, "E9.4.5.0", {"start": v(39.58, -23.24) * mm, "end": v(39.58, -22.29) * mm});
            skLineSegment(sketch, "E9.4.5.1", {"start": v(28.08, -23.24) * mm, "end": v(39.58, -23.24) * mm});
            skLineSegment(sketch, "E9.4.5.2", {"start": v(45.08, -22.29) * mm, "end": v(45.08, -13.53) * mm});
            skLineSegment(sketch, "E9.4.5.3", {"start": v(39.58, -13.53) * mm, "end": v(39.58, -12.57) * mm});
            skLineSegment(sketch, "E9.4.5.4", {"start": v(39.58, -22.29) * mm, "end": v(45.08, -22.29) * mm});
            skLineSegment(sketch, "E9.4.5.5", {"start": v(28.08, -12.57) * mm, "end": v(28.08, -23.24) * mm});
            skLineSegment(sketch, "E9.4.5.6", {"start": v(39.58, -12.57) * mm, "end": v(28.08, -12.57) * mm});
            skLineSegment(sketch, "E9.4.5.7", {"start": v(45.08, -13.53) * mm, "end": v(39.58, -13.53) * mm});
            skLineSegment(sketch, "E9.4.6.0", {"start": v(39.58, -35.18) * mm, "end": v(39.58, -34.23) * mm});
            skLineSegment(sketch, "E9.4.6.1", {"start": v(28.08, -35.18) * mm, "end": v(39.58, -35.18) * mm});
            skLineSegment(sketch, "E9.4.6.2", {"start": v(45.08, -34.23) * mm, "end": v(45.08, -25.46) * mm});
            skLineSegment(sketch, "E9.4.6.3", {"start": v(39.58, -25.46) * mm, "end": v(39.58, -24.51) * mm});
            skLineSegment(sketch, "E9.4.6.4", {"start": v(39.58, -34.23) * mm, "end": v(45.08, -34.23) * mm});
            skLineSegment(sketch, "E9.4.6.5", {"start": v(28.08, -24.51) * mm, "end": v(28.08, -35.18) * mm});
            skLineSegment(sketch, "E9.4.6.6", {"start": v(39.58, -24.51) * mm, "end": v(28.08, -24.51) * mm});
            skLineSegment(sketch, "E9.4.6.7", {"start": v(45.08, -25.46) * mm, "end": v(39.58, -25.46) * mm});
            skLineSegment(sketch, "E9.4.7.0", {"start": v(39.58, -47.12) * mm, "end": v(39.58, -46.16) * mm});
            skLineSegment(sketch, "E9.4.7.1", {"start": v(28.08, -47.12) * mm, "end": v(39.58, -47.12) * mm});
            skLineSegment(sketch, "E9.4.7.2", {"start": v(45.08, -46.16) * mm, "end": v(45.08, -37.4) * mm});
            skLineSegment(sketch, "E9.4.7.3", {"start": v(39.58, -37.4) * mm, "end": v(39.58, -36.45) * mm});
            skLineSegment(sketch, "E9.4.7.4", {"start": v(39.58, -46.16) * mm, "end": v(45.08, -46.16) * mm});
            skLineSegment(sketch, "E9.4.7.5", {"start": v(28.08, -36.45) * mm, "end": v(28.08, -47.12) * mm});
            skLineSegment(sketch, "E9.4.7.6", {"start": v(39.58, -36.45) * mm, "end": v(28.08, -36.45) * mm});
            skLineSegment(sketch, "E9.4.7.7", {"start": v(45.08, -37.4) * mm, "end": v(39.58, -37.4) * mm});
            skLineSegment(sketch, "E9.direction1", {"start": v(-45.07, 47.12) * mm, "end": v(-26.79, 47.12) * mm, "construction": true});
            skLineSegment(sketch, "E9.direction2", {"start": v(-45.07, 47.12) * mm, "end": v(-45.07, 35.18) * mm, "construction": true});
            skSolve(sketch);
        }
        {
            var Q0;
            Q0=makeQuery(id+"F0.imprint","IMPRINT",FACE,{"disambiguationData":[TD([[makeQuery(id+"F0.imprint","IMPRINT",EDGE,{"derivedFrom":sQuery(id+"F0.wireOp",EDGE,"E0.bottom")}),-1.0]])]});
            extrude(context, id + "F1", {"entities" : qUnion([Q0]), "depth" : 5 * mm});
        }
        {
            var Q0;
            Q0=makeQuery(id+"F0.imprint","IMPRINT",FACE,{"disambiguationData":[TD([[makeQuery(id+"F0.imprint","IMPRINT",EDGE,{"derivedFrom":sQuery(id+"F0.wireOp",EDGE,"E9.2.5.0")}),1.0]])]});
            var Q1;
            Q1=makeQuery(id+"F0.imprint","IMPRINT",FACE,{"disambiguationData":[TD([[makeQuery(id+"F0.imprint","IMPRINT",EDGE,{"derivedFrom":sQuery(id+"F0.wireOp",EDGE,"E9.4.4.0")}),1.0]])]});
            var Q2;
            Q2=makeQuery(id+"F0.imprint","IMPRINT",FACE,{"disambiguationData":[TD([[makeQuery(id+"F0.imprint","IMPRINT",EDGE,{"derivedFrom":sQuery(id+"F0.wireOp",EDGE,"E9.1.2.0")}),1.0]])]});
            var Q3;
            Q3=makeQuery(id+"F0.imprint","IMPRINT",FACE,{"disambiguationData":[TD([[makeQuery(id+"F0.imprint","IMPRINT",EDGE,{"derivedFrom":sQuery(id+"F0.wireOp",EDGE,"E9.3.6.0")}),1.0]])]});
            var Q4;
            Q4=makeQuery(id+"F0.imprint","IMPRINT",FACE,{"disambiguationData":[TD([[makeQuery(id+"F0.imprint","IMPRINT",EDGE,{"derivedFrom":sQuery(id+"F0.wireOp",EDGE,"E9.2.1.0")}),1.0]])]});
            var Q5;
            Q5=makeQuery(id+"F0.imprint","IMPRINT",FACE,{"disambiguationData":[TD([[makeQuery(id+"F0.imprint","IMPRINT",EDGE,{"derivedFrom":sQuery(id+"F0.wireOp",EDGE,"E9.5.0.0")}),1.0]])]});
            var Q6;
            Q6=makeQuery(id+"F0.imprint","IMPRINT",FACE,{"disambiguationData":[TD([[makeQuery(id+"F0.imprint","IMPRINT",EDGE,{"derivedFrom":sQuery(id+"F0.wireOp",EDGE,"E9.0.7.0")}),1.0]])]});
            var Q7;
            Q7=makeQuery(id+"F0.imprint","IMPRINT",FACE,{"disambiguationData":[TD([[makeQuery(id+"F0.imprint","IMPRINT",EDGE,{"derivedFrom":sQuery(id+"F0.wireOp",EDGE,"E9.0.2.0")}),1.0]])]});
            var Q8;
            Q8=makeQuery(id+"F0.imprint","IMPRINT",FACE,{"disambiguationData":[TD([[makeQuery(id+"F0.imprint","IMPRINT",EDGE,{"derivedFrom":sQuery(id+"F0.wireOp",EDGE,"E9.4.5.0")}),1.0]])]});
            var Q9;
            Q9=makeQuery(id+"F0.imprint","IMPRINT",FACE,{"disambiguationData":[TD([[makeQuery(id+"F0.imprint","IMPRINT",EDGE,{"derivedFrom":sQuery(id+"F0.wireOp",EDGE,"E9.5.3.0")}),1.0]])]});
            var Q10;
            Q10=makeQuery(id+"F0.imprint","IMPRINT",FACE,{"disambiguationData":[TD([[makeQuery(id+"F0.imprint","IMPRINT",EDGE,{"derivedFrom":sQuery(id+"F0.wireOp",EDGE,"E9.3.1.0")}),1.0]])]});
            var Q11;
            Q11=makeQuery(id+"F0.imprint","IMPRINT",FACE,{"disambiguationData":[TD([[makeQuery(id+"F0.imprint","IMPRINT",EDGE,{"derivedFrom":sQuery(id+"F0.wireOp",EDGE,"E9.4.1.0")}),1.0]])]});
            var Q12;
            Q12=makeQuery(id+"F0.imprint","IMPRINT",FACE,{"disambiguationData":[TD([[makeQuery(id+"F0.imprint","IMPRINT",EDGE,{"derivedFrom":sQuery(id+"F0.wireOp",EDGE,"E9.4.3.0")}),1.0]])]});
            var Q13;
            Q13=makeQuery(id+"F0.imprint","IMPRINT",FACE,{"disambiguationData":[TD([[makeQuery(id+"F0.imprint","IMPRINT",EDGE,{"derivedFrom":sQuery(id+"F0.wireOp",EDGE,"E9.1.5.0")}),1.0]])]});
            var Q14;
            Q14=makeQuery(id+"F0.imprint","IMPRINT",FACE,{"disambiguationData":[TD([[makeQuery(id+"F0.imprint","IMPRINT",EDGE,{"derivedFrom":sQuery(id+"F0.wireOp",EDGE,"E9.0.6.0")}),1.0]])]});
            var Q15;
            Q15=makeQuery(id+"F0.imprint","IMPRINT",FACE,{"disambiguationData":[TD([[makeQuery(id+"F0.imprint","IMPRINT",EDGE,{"derivedFrom":sQuery(id+"F0.wireOp",EDGE,"E9.2.4.0")}),1.0]])]});
            var Q16;
            Q16=makeQuery(id+"F0.imprint","IMPRINT",FACE,{"disambiguationData":[TD([[makeQuery(id+"F0.imprint","IMPRINT",EDGE,{"derivedFrom":sQuery(id+"F0.wireOp",EDGE,"E9.0.4.0")}),1.0]])]});
            var Q17;
            Q17=makeQuery(id+"F0.imprint","IMPRINT",FACE,{"disambiguationData":[TD([[makeQuery(id+"F0.imprint","IMPRINT",EDGE,{"derivedFrom":sQuery(id+"F0.wireOp",EDGE,"E9.0.3.0")}),1.0]])]});
            var Q18;
            Q18=makeQuery(id+"F0.imprint","IMPRINT",FACE,{"disambiguationData":[TD([[makeQuery(id+"F0.imprint","IMPRINT",EDGE,{"derivedFrom":sQuery(id+"F0.wireOp",EDGE,"E9.5.4.0")}),1.0]])]});
            var Q19;
            Q19=makeQuery(id+"F0.imprint","IMPRINT",FACE,{"disambiguationData":[TD([[makeQuery(id+"F0.imprint","IMPRINT",EDGE,{"derivedFrom":sQuery(id+"F0.wireOp",EDGE,"E9.1.4.0")}),1.0]])]});
            var Q20;
            Q20=makeQuery(id+"F0.imprint","IMPRINT",FACE,{"disambiguationData":[TD([[makeQuery(id+"F0.imprint","IMPRINT",EDGE,{"derivedFrom":sQuery(id+"F0.wireOp",EDGE,"E9.4.6.0")}),1.0]])]});
            var Q21;
            Q21=makeQuery(id+"F0.imprint","IMPRINT",FACE,{"disambiguationData":[TD([[makeQuery(id+"F0.imprint","IMPRINT",EDGE,{"derivedFrom":sQuery(id+"F0.wireOp",EDGE,"E9.3.2.0")}),1.0]])]});
            var Q22;
            Q22=makeQuery(id+"F0.imprint","IMPRINT",FACE,{"disambiguationData":[TD([[makeQuery(id+"F0.imprint","IMPRINT",EDGE,{"derivedFrom":sQuery(id+"F0.wireOp",EDGE,"E9.1.6.0")}),1.0]])]});
            var Q23;
            Q23=makeQuery(id+"F0.imprint","IMPRINT",FACE,{"disambiguationData":[TD([[makeQuery(id+"F0.imprint","IMPRINT",EDGE,{"derivedFrom":sQuery(id+"F0.wireOp",EDGE,"E9.3.0.0")}),1.0]])]});
            var Q24;
            Q24=makeQuery(id+"F0.imprint","IMPRINT",FACE,{"disambiguationData":[TD([[makeQuery(id+"F0.imprint","IMPRINT",EDGE,{"derivedFrom":sQuery(id+"F0.wireOp",EDGE,"E9.5.2.0")}),1.0]])]});
            var Q25;
            Q25=makeQuery(id+"F0.imprint","IMPRINT",FACE,{"disambiguationData":[TD([[makeQuery(id+"F0.imprint","IMPRINT",EDGE,{"derivedFrom":sQuery(id+"F0.wireOp",EDGE,"E9.2.7.0")}),1.0]])]});
            var Q26;
            Q26=makeQuery(id+"F0.imprint","IMPRINT",FACE,{"disambiguationData":[TD([[makeQuery(id+"F0.imprint","IMPRINT",EDGE,{"derivedFrom":sQuery(id+"F0.wireOp",EDGE,"E9.3.3.0")}),1.0]])]});
            var Q27;
            Q27=makeQuery(id+"F0.imprint","IMPRINT",FACE,{"disambiguationData":[TD([[makeQuery(id+"F0.imprint","IMPRINT",EDGE,{"derivedFrom":sQuery(id+"F0.wireOp",EDGE,"E9.5.1.0")}),1.0]])]});
            var Q28;
            Q28=makeQuery(id+"F0.imprint","IMPRINT",FACE,{"disambiguationData":[TD([[makeQuery(id+"F0.imprint","IMPRINT",EDGE,{"derivedFrom":sQuery(id+"F0.wireOp",EDGE,"E9.1.7.0")}),1.0]])]});
            var Q29;
            Q29=makeQuery(id+"F0.imprint","IMPRINT",FACE,{"disambiguationData":[TD([[makeQuery(id+"F0.imprint","IMPRINT",EDGE,{"derivedFrom":sQuery(id+"F0.wireOp",EDGE,"E9.1.0.0")}),1.0]])]});
            var Q30;
            Q30=makeQuery(id+"F0.imprint","IMPRINT",FACE,{"disambiguationData":[TD([[makeQuery(id+"F0.imprint","IMPRINT",EDGE,{"derivedFrom":sQuery(id+"F0.wireOp",EDGE,"E9.5.6.0")}),1.0]])]});
            var Q31;
            Q31=makeQuery(id+"F0.imprint","IMPRINT",FACE,{"disambiguationData":[TD([[makeQuery(id+"F0.imprint","IMPRINT",EDGE,{"derivedFrom":sQuery(id+"F0.wireOp",EDGE,"E9.0.5.0")}),1.0]])]});
            var Q32;
            Q32=makeQuery(id+"F0.imprint","IMPRINT",FACE,{"disambiguationData":[TD([[makeQuery(id+"F0.imprint","IMPRINT",EDGE,{"derivedFrom":sQuery(id+"F0.wireOp",EDGE,"E9.4.7.0")}),1.0]])]});
            var Q33;
            Q33=makeQuery(id+"F0.imprint","IMPRINT",FACE,{"disambiguationData":[TD([[makeQuery(id+"F0.imprint","IMPRINT",EDGE,{"derivedFrom":sQuery(id+"F0.wireOp",EDGE,"E9.4.0.0")}),1.0]])]});
            var Q34;
            Q34=makeQuery(id+"F0.imprint","IMPRINT",FACE,{"disambiguationData":[TD([[makeQuery(id+"F0.imprint","IMPRINT",EDGE,{"derivedFrom":sQuery(id+"F0.wireOp",EDGE,"E9.5.5.0")}),1.0]])]});
            var Q35;
            Q35=makeQuery(id+"F0.imprint","IMPRINT",FACE,{"disambiguationData":[TD([[makeQuery(id+"F0.imprint","IMPRINT",EDGE,{"derivedFrom":sQuery(id+"F0.wireOp",EDGE,"E9.5.7.0")}),1.0]])]});
            var Q36;
            Q36=makeQuery(id+"F0.imprint","IMPRINT",FACE,{"disambiguationData":[TD([[makeQuery(id+"F0.imprint","IMPRINT",EDGE,{"derivedFrom":sQuery(id+"F0.wireOp",EDGE,"E9.1.3.0")}),1.0]])]});
            var Q37;
            Q37=makeQuery(id+"F0.imprint","IMPRINT",FACE,{"disambiguationData":[TD([[makeQuery(id+"F0.imprint","IMPRINT",EDGE,{"derivedFrom":sQuery(id+"F0.wireOp",EDGE,"E9.2.3.0")}),1.0]])]});
            var Q38;
            Q38=makeQuery(id+"F0.imprint","IMPRINT",FACE,{"disambiguationData":[TD([[makeQuery(id+"F0.imprint","IMPRINT",EDGE,{"derivedFrom":sQuery(id+"F0.wireOp",EDGE,"E9.1.1.0")}),1.0]])]});
            var Q39;
            Q39=makeQuery(id+"F0.imprint","IMPRINT",FACE,{"disambiguationData":[TD([[makeQuery(id+"F0.imprint","IMPRINT",EDGE,{"derivedFrom":sQuery(id+"F0.wireOp",EDGE,"E9.4.2.0")}),1.0]])]});
            var Q40;
            Q40=makeQuery(id+"F0.imprint","IMPRINT",FACE,{"disambiguationData":[TD([[makeQuery(id+"F0.imprint","IMPRINT",EDGE,{"derivedFrom":sQuery(id+"F0.wireOp",EDGE,"E9.3.4.0")}),1.0]])]});
            var Q41;
            Q41=makeQuery(id+"F0.imprint","IMPRINT",FACE,{"disambiguationData":[TD([[makeQuery(id+"F0.imprint","IMPRINT",EDGE,{"derivedFrom":sQuery(id+"F0.wireOp",EDGE,"E9.0.1.0")}),1.0]])]});
            var Q42;
            Q42=makeQuery(id+"F0.imprint","IMPRINT",FACE,{"disambiguationData":[TD([[makeQuery(id+"F0.imprint","IMPRINT",EDGE,{"derivedFrom":sQuery(id+"F0.wireOp",EDGE,"E9.2.2.0")}),1.0]])]});
            var Q43;
            Q43=makeQuery(id+"F0.imprint","IMPRINT",FACE,{"disambiguationData":[TD([[makeQuery(id+"F0.imprint","IMPRINT",EDGE,{"derivedFrom":sQuery(id+"F0.wireOp",EDGE,"E9.3.7.0")}),1.0]])]});
            var Q44;
            Q44=makeQuery(id+"F0.imprint","IMPRINT",FACE,{"disambiguationData":[TD([[makeQuery(id+"F0.imprint","IMPRINT",EDGE,{"derivedFrom":sQuery(id+"F0.wireOp",EDGE,"E9.2.6.0")}),1.0]])]});
            var Q45;
            Q45=makeQuery(id+"F0.imprint","IMPRINT",FACE,{"disambiguationData":[TD([[makeQuery(id+"F0.imprint","IMPRINT",EDGE,{"derivedFrom":sQuery(id+"F0.wireOp",EDGE,"E1")}),1.0]])]});
            var Q46;
            Q46=makeQuery(id+"F0.imprint","IMPRINT",FACE,{"disambiguationData":[TD([[makeQuery(id+"F0.imprint","IMPRINT",EDGE,{"derivedFrom":sQuery(id+"F0.wireOp",EDGE,"E9.2.0.0")}),1.0]])]});
            var Q47;
            Q47=makeQuery(id+"F0.imprint","IMPRINT",FACE,{"disambiguationData":[TD([[makeQuery(id+"F0.imprint","IMPRINT",EDGE,{"derivedFrom":sQuery(id+"F0.wireOp",EDGE,"E9.3.5.0")}),1.0]])]});
            extrude(context, id + "F2", {"entities" : qUnion([Q0, Q1, Q2, Q3, Q4, Q5, Q6, Q7, Q8, Q9, Q10, Q11, Q12, Q13, Q14, Q15, Q16, Q17, Q18, Q19, Q20, Q21, Q22, Q23, Q24, Q25, Q26, Q27, Q28, Q29, Q30, Q31, Q32, Q33, Q34, Q35, Q36, Q37, Q38, Q39, Q40, Q41, Q42, Q43, Q44, Q45, Q46, Q47]), "operationType" : NewBodyOperationType.ADD, "depth" : 2.5 * mm});
        }
    });
